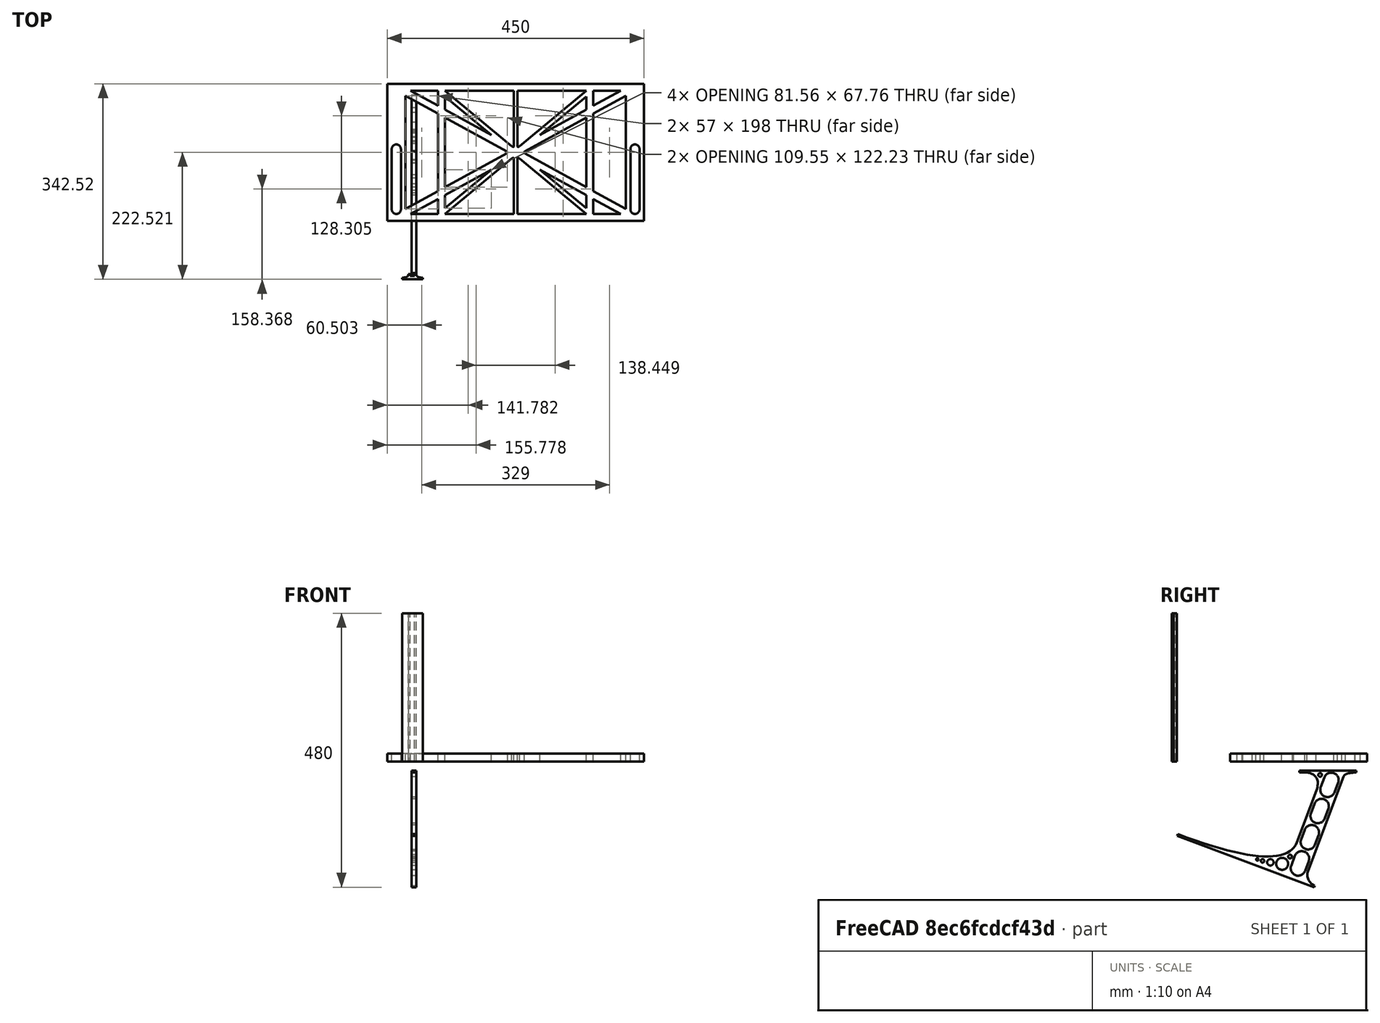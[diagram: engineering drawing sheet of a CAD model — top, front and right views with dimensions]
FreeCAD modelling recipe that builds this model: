
FCSTD DOCUMENT  (FreeCAD 0.19R0.19.2)
Label: laptopStand062
License: All rights reserved
LicenseURL: http://en.wikipedia.org/wiki/All_rights_reserved
objects: Sketcher::SketchObject×3, Part::Extrusion×3
note: 6 computed .brp shape members not serialized (recipe doc carries the construction recipe); baked Part::Feature solids carry a one-line shape summary decoded from their .brp

FEATURE [Sketcher::SketchObject] Sketch
  FullyConstrained = false
  sketch-geometry (100):
    g0: LineSegment StartX=375.073 StartY=115.221 StartZ=0 EndX=318.073 EndY=83.9235 EndZ=0
    g1: LineSegment StartX=-10.9272 StartY=-82.7794 StartZ=0 EndX=46.0728 EndY=-51.4823 EndZ=0
    g2: LineSegment StartX=366.073 StartY=-91.7794 StartZ=0 EndX=318.073 EndY=-65.424 EndZ=0
    g3: LineSegment StartX=-10.9272 StartY=77.3346 StartZ=0 EndX=-10.9272 EndY=-82.7794 EndZ=0
    g4: LineSegment StartX=375.073 StartY=-82.7794 StartZ=0 EndX=375.073 EndY=115.221 EndZ=0
    g5: LineSegment StartX=-1.92719 StartY=-91.7794 StartZ=0 EndX=46.0728 EndY=-91.7794 EndZ=0
    g6: LineSegment StartX=318.073 StartY=124.221 StartZ=0 EndX=366.073 EndY=124.221 EndZ=0
    g7: LineSegment StartX=306.073 StartY=-81.8102 StartZ=0 EndX=224.513 EndY=-14.0532 EndZ=0
    g8: LineSegment StartX=58.0728 StartY=114.251 StartZ=0 EndX=139.632 EndY=46.4944 EndZ=0
    g9: LineSegment StartX=306.073 StartY=124.221 StartZ=0 EndX=189.124 EndY=27.0628 EndZ=0
    g10: LineSegment StartX=58.0728 StartY=-91.7794 StartZ=0 EndX=175.022 EndY=5.37834 EndZ=0
    g11: LineSegment StartX=58.0728 StartY=-81.8102 StartZ=0 EndX=58.0728 EndY=-58.8351 EndZ=0
    g12: LineSegment StartX=318.073 StartY=124.221 StartZ=0 EndX=318.073 EndY=97.8651 EndZ=0
    g13: LineSegment StartX=306.073 StartY=114.251 StartZ=0 EndX=306.073 EndY=91.2763 EndZ=0
    g14: LineSegment StartX=224.513 StartY=46.4944 StartZ=0 EndX=306.073 EndY=114.251 EndZ=0
    g15: LineSegment StartX=175.022 StartY=27.0628 StartZ=0 EndX=58.0728 EndY=124.221 EndZ=0
    g16: LineSegment StartX=139.632 StartY=-14.0532 StartZ=0 EndX=58.0728 EndY=-81.8102 EndZ=0
    g17: LineSegment StartX=224.513 StartY=46.4944 StartZ=0 EndX=306.073 EndY=91.2763 EndZ=0
    g18: LineSegment StartX=139.632 StartY=-14.0532 StartZ=0 EndX=58.0728 EndY=-58.8351 EndZ=0
    g19: LineSegment StartX=189.124 StartY=5.37834 StartZ=0 EndX=306.073 EndY=-91.7794 EndZ=0
    g20: LineSegment StartX=306.073 StartY=77.3346 StartZ=0 EndX=306.073 EndY=-44.8935 EndZ=0
    g21: LineSegment StartX=318.073 StartY=83.9235 StartZ=0 EndX=318.073 EndY=-51.4823 EndZ=0
    g22: LineSegment StartX=318.073 StartY=97.8651 StartZ=0 EndX=366.073 EndY=124.221 EndZ=0
    g23: LineSegment StartX=306.073 StartY=-58.8351 StartZ=0 EndX=224.513 EndY=-14.0532 EndZ=0
    g24: LineSegment StartX=306.073 StartY=-58.8351 StartZ=0 EndX=306.073 EndY=-81.8102 EndZ=0
    g25: LineSegment StartX=318.073 StartY=-51.4823 StartZ=0 EndX=375.073 EndY=-82.7794 EndZ=0
    g26: LineSegment StartX=318.073 StartY=-65.424 StartZ=0 EndX=318.073 EndY=-91.7794 EndZ=0
    g27: LineSegment StartX=318.073 StartY=-91.7794 StartZ=0 EndX=366.073 EndY=-91.7794 EndZ=0
    g28: LineSegment StartX=58.0728 StartY=-44.8935 StartZ=0 EndX=58.0728 EndY=77.3346 EndZ=0
    g29: LineSegment StartX=46.0728 StartY=-65.424 StartZ=0 EndX=-1.92719 EndY=-91.7794 EndZ=0
    g30: LineSegment StartX=46.0728 StartY=-65.424 StartZ=0 EndX=46.0728 EndY=-91.7794 EndZ=0
    g31: LineSegment StartX=58.0728 StartY=91.2763 StartZ=0 EndX=58.0728 EndY=114.251 EndZ=0
    g32: LineSegment StartX=46.0728 StartY=77.3346 StartZ=0 EndX=46.0728 EndY=-51.4823 EndZ=0
    g33: LineSegment StartX=58.0728 StartY=91.2763 StartZ=0 EndX=139.632 EndY=46.4944 EndZ=0
    g34: LineSegment StartX=-42.9272 StartY=136.221 StartZ=0 EndX=-42.9272 EndY=-103.779 EndZ=0
    g35: LineSegment StartX=407.073 StartY=136.221 StartZ=0 EndX=407.073 EndY=-103.779 EndZ=0
    g36: LineSegment StartX=179.022 StartY=27.0628 StartZ=0 EndX=179.022 EndY=124.221 EndZ=0
    g37: LineSegment StartX=185.124 StartY=27.0628 StartZ=0 EndX=185.124 EndY=124.221 EndZ=0
    g38: ArcOfCircle CenterX=-26.9272 CenterY=22.1087 CenterZ=0 NormalX=0 NormalY=0 NormalZ=1 AngleXU=0 Radius=8 StartAngle=1e-16 EndAngle=3.14159
    g39: ArcOfCircle CenterX=-26.9272 CenterY=-83.7794 CenterZ=0 NormalX=0 NormalY=0 NormalZ=1 AngleXU=0 Radius=8 StartAngle=3.14159 EndAngle=6.28319
    g40: LineSegment StartX=-34.9272 StartY=22.1087 StartZ=0 EndX=-34.9272 EndY=-83.7794 EndZ=0
    g41: LineSegment StartX=-18.9272 StartY=22.1087 StartZ=0 EndX=-18.9272 EndY=-83.7794 EndZ=0
    g42: LineSegment StartX=185.124 StartY=-91.7794 StartZ=0 EndX=306.073 EndY=-91.7794 EndZ=0
    g43: LineSegment StartX=179.022 StartY=-91.7794 StartZ=0 EndX=58.0728 EndY=-91.7794 EndZ=0
    g44: LineSegment StartX=306.073 StartY=124.221 StartZ=0 EndX=185.124 EndY=124.221 EndZ=0
    g45: LineSegment StartX=179.022 StartY=124.221 StartZ=0 EndX=58.0728 EndY=124.221 EndZ=0
    g46: ArcOfCircle CenterX=391.073 CenterY=22.1087 CenterZ=0 NormalX=0 NormalY=0 NormalZ=1 AngleXU=0 Radius=8 StartAngle=-4.4e-15 EndAngle=3.14159
    g47: LineSegment StartX=399.073 StartY=22.1087 StartZ=0 EndX=399.073 EndY=-83.7794 EndZ=0
    g48: LineSegment StartX=383.073 StartY=22.1087 StartZ=0 EndX=383.073 EndY=-83.7794 EndZ=0
    g49: ArcOfCircle CenterX=391.073 CenterY=-83.7794 CenterZ=0 NormalX=0 NormalY=0 NormalZ=1 AngleXU=0 Radius=8 StartAngle=3.14159 EndAngle=6.28319
    g50: Circle CenterX=175.022 CenterY=27.0628 CenterZ=0 NormalX=0 NormalY=0 NormalZ=1 AngleXU=0 Radius=1
    g51: Circle CenterX=179.022 CenterY=24.8665 CenterZ=0 NormalX=0 NormalY=0 NormalZ=1 AngleXU=0 Radius=1
    g52: Circle CenterX=179.022 CenterY=27.0628 CenterZ=0 NormalX=0 NormalY=0 NormalZ=1 AngleXU=0 Radius=1
    g53: BSplineCurve PolesCount=3 KnotsCount=2 Degree=2 IsPeriodic=0
    g54: GeomPoint X=175.022 Y=27.0628 Z=0
    g55: GeomPoint X=179.022 Y=27.0628 Z=0
    g56: Circle CenterX=189.124 CenterY=27.0628 CenterZ=0 NormalX=0 NormalY=0 NormalZ=1 AngleXU=0 Radius=1
    g57: Circle CenterX=185.124 CenterY=24.8665 CenterZ=0 NormalX=0 NormalY=0 NormalZ=1 AngleXU=0 Radius=1
    g58: Circle CenterX=185.124 CenterY=27.0628 CenterZ=0 NormalX=0 NormalY=0 NormalZ=1 AngleXU=0 Radius=1
    g59: BSplineCurve PolesCount=3 KnotsCount=2 Degree=2 IsPeriodic=0
    g60: GeomPoint X=189.124 Y=27.0628 Z=0
    g61: GeomPoint X=185.124 Y=27.0628 Z=0
    g62: Circle CenterX=175.022 CenterY=5.37834 CenterZ=0 NormalX=0 NormalY=0 NormalZ=1 AngleXU=0 Radius=1
    g63: Circle CenterX=179.022 CenterY=7.57463 CenterZ=0 NormalX=0 NormalY=0 NormalZ=1 AngleXU=0 Radius=1
    g64: Circle CenterX=179.022 CenterY=5.34704 CenterZ=0 NormalX=0 NormalY=0 NormalZ=1 AngleXU=0 Radius=1
    g65: BSplineCurve PolesCount=3 KnotsCount=2 Degree=2 IsPeriodic=0
    g66: GeomPoint X=175.022 Y=5.37834 Z=0
    g67: GeomPoint X=179.022 Y=5.34704 Z=0
    g68: Circle CenterX=189.124 CenterY=5.37834 CenterZ=0 NormalX=0 NormalY=0 NormalZ=1 AngleXU=0 Radius=1
    g69: Circle CenterX=185.124 CenterY=7.57463 CenterZ=0 NormalX=0 NormalY=0 NormalZ=1 AngleXU=0 Radius=1
    g70: Circle CenterX=185.124 CenterY=5.34704 CenterZ=0 NormalX=0 NormalY=0 NormalZ=1 AngleXU=0 Radius=1
    g71: BSplineCurve PolesCount=3 KnotsCount=2 Degree=2 IsPeriodic=0
    g72: GeomPoint X=189.124 Y=5.37834 Z=0
    g73: GeomPoint X=185.124 Y=5.34704 Z=0
    g74: LineSegment StartX=179.022 StartY=5.34704 StartZ=0 EndX=179.022 EndY=-91.7794 EndZ=0
    g75: LineSegment StartX=185.124 StartY=-91.7794 StartZ=0 EndX=185.124 EndY=5.34704 EndZ=0
    g76: Circle CenterX=165.871 CenterY=18.1458 CenterZ=0 NormalX=0 NormalY=0 NormalZ=1 AngleXU=0 Radius=1
    g77: Circle CenterX=169.377 CenterY=16.2206 CenterZ=0 NormalX=0 NormalY=0 NormalZ=1 AngleXU=0 Radius=1
    g78: Circle CenterX=165.871 CenterY=14.2954 CenterZ=0 NormalX=0 NormalY=0 NormalZ=1 AngleXU=0 Radius=1
    g79: BSplineCurve PolesCount=3 KnotsCount=2 Degree=2 IsPeriodic=0
    g80: GeomPoint X=165.871 Y=18.1458 Z=0
    g81: GeomPoint X=165.871 Y=14.2954 Z=0
    g82: Circle CenterX=198.275 CenterY=18.1458 CenterZ=0 NormalX=0 NormalY=0 NormalZ=1 AngleXU=0 Radius=1
    g83: Circle CenterX=194.768 CenterY=16.2206 CenterZ=0 NormalX=0 NormalY=0 NormalZ=1 AngleXU=0 Radius=1
    g84: Circle CenterX=198.275 CenterY=14.2954 CenterZ=0 NormalX=0 NormalY=0 NormalZ=1 AngleXU=0 Radius=1
    g85: BSplineCurve PolesCount=3 KnotsCount=2 Degree=2 IsPeriodic=0
    g86: GeomPoint X=198.275 Y=18.1458 Z=0
    g87: GeomPoint X=198.275 Y=14.2954 Z=0
    g88: LineSegment StartX=165.871 StartY=18.1458 StartZ=0 EndX=58.0728 EndY=77.3346 EndZ=0
    g89: LineSegment StartX=58.0728 StartY=-44.8935 StartZ=0 EndX=165.871 EndY=14.2954 EndZ=0
    g90: LineSegment StartX=198.275 StartY=18.1458 StartZ=0 EndX=306.073 EndY=77.3346 EndZ=0
    g91: LineSegment StartX=198.275 StartY=14.2954 StartZ=0 EndX=306.073 EndY=-44.8935 EndZ=0
    g92: LineSegment StartX=407.073 StartY=-103.779 StartZ=0 EndX=-42.9272 EndY=-103.779 EndZ=0
    g93: LineSegment StartX=407.073 StartY=136.221 StartZ=0 EndX=-42.9272 EndY=136.221 EndZ=0
    g94: LineSegment StartX=-26.9272 StartY=136.221 StartZ=0 EndX=-26.9272 EndY=98.2206 EndZ=0
    g95: LineSegment StartX=46.0728 StartY=77.3346 StartZ=0 EndX=-10.9272 EndY=77.3346 EndZ=0
    g96: LineSegment StartX=46.0728 StartY=105.865 StartZ=0 EndX=31.5028 EndY=105.865 EndZ=0
    g97: LineSegment StartX=46.0728 StartY=124.221 StartZ=0 EndX=46.0728 EndY=105.865 EndZ=0
    g98: LineSegment StartX=-1.92719 StartY=124.221 StartZ=0 EndX=31.5028 EndY=105.865 EndZ=0
    g99: LineSegment StartX=46.0728 StartY=124.221 StartZ=0 EndX=-1.92719 EndY=124.221 EndZ=0
  constraints (185):
    c: Horizontal(g5)
    c: Horizontal(g6)
    c: Coincident(g33,g8)
    c: Coincident(g14,g17)
    c: Coincident(g18,g16)
    c: Coincident(g23,g7)
    c: Coincident(g14,g13)
    c: Tangent(g13,g20)
    c: Tangent(g12,g21)
    c: Coincident(g17,g13)
    c: Tangent(g17,g22)
    c: Coincident(g0,g21)
    c: Coincident(g24,g7)
    c: Tangent(g2,g23)
    c: Tangent(g20,g24)
    c: Coincident(g21,g25)
    c: Coincident(g26,g2)
    c: Tangent(g21,g26)
    c: Coincident(g16,g11)
    c: Tangent(g11,g28)
    c: Coincident(g18,g11)
    c: Tangent(g18,g29)
    c: Coincident(g30,g29)
    c: Coincident(g1,g32)
    c: Tangent(g28,g31)
    c: Coincident(g8,g31)
    c: Coincident(g33,g31)
    c: Block(g15)
    c: Block(g9)
    c: Block(g12)
    c: Block(g22)
    c: Block(g0)
    c: Block(g25)
    c: Block(g4)
    c: Block(g23)
    c: Block(g24)
    c: Block(g2)
    c: Block(g26)
    c: Block(g14)
    c: Block(g19)
    c: Block(g10)
    c: Block(g18)
    c: Block(g16)
    c: Block(g30)
    c: Block(g29)
    c: Block(g1)
    c: Block(g3)
    c: Block(g8)
    c: Block(g31)
    c: Block(g20)
    c: Block(g6)
    c: Block(g27)
    c: Block(g5)
    c: Vertical(g34)
    c: Vertical(g35)
    c: Block(g35)
    c: Block(g34)
    c: Vertical(g36)
    c: Vertical(g37)
    c: Block(g36)
    c: Block(g37)
    c: Tangent(g38,g41) = 1.5708
    c: Tangent(g38,g40) = -1.5708
    c: Tangent(g40,g39) = -1.5708
    c: Tangent(g41,g39) = 1.5708
    c: Vertical(g40)
    c: Equal(g38,g39)
    c: Block(g41)
    c: Block(g40)
    c: Coincident(g42,g19)
    c: Horizontal(g42)
    c: Coincident(g43,g10)
    c: Horizontal(g43)
    c: Coincident(g44,g9)
    c: Coincident(g44,g37)
    c: Horizontal(g44)
    c: Coincident(g45,g36)
    c: Coincident(g45,g15)
    c: Horizontal(g45)
    c: Tangent(g46,g47) = 1.5708
    c: Tangent(g47,g49) = 1.5708
    c: Equal(g46,g49)
    c: Coincident(g48,g46)
    c: Coincident(g48,g49)
    c: Block(g47)
    c: Block(g48)
    c: Coincident(g53,g15)
    c: Weight(g50) = 1
    c: Equal(g50,g51)
    c: Equal(g50,g52)
    c: Coincident(g53,g36)
    c: InternalAlignment(g50,g53)
    c: InternalAlignment(g51,g53)
    c: InternalAlignment(g52,g53)
    c: InternalAlignment(g54,g53)
    c: InternalAlignment(g55,g53)
    c: Coincident(g59,g9)
    c: Weight(g56) = 1
    c: Equal(g56,g57)
    c: Equal(g56,g58)
    c: Coincident(g59,g37)
    c: InternalAlignment(g56,g59)
    c: InternalAlignment(g57,g59)
    c: InternalAlignment(g58,g59)
    c: InternalAlignment(g60,g59)
    c: InternalAlignment(g61,g59)
    c: Block(g59)
    c: Block(g53)
    c: Coincident(g65,g10)
    c: Weight(g62) = 1
    c: Equal(g62,g63)
    c: Equal(g62,g64)
    c: InternalAlignment(g62,g65)
    c: InternalAlignment(g63,g65)
    c: InternalAlignment(g64,g65)
    c: InternalAlignment(g66,g65)
    c: InternalAlignment(g67,g65)
    c: Weight(g68) = 1
    c: Equal(g68,g69)
    c: Equal(g68,g70)
    c: InternalAlignment(g68,g71)
    c: InternalAlignment(g69,g71)
    c: InternalAlignment(g70,g71)
    c: InternalAlignment(g72,g71)
    c: InternalAlignment(g73,g71)
    c: Block(g71)
    c: Block(g65)
    c: Coincident(g74,g65)
    c: Coincident(g74,g43)
    c: Vertical(g74)
    c: Coincident(g75,g42)
    c: Coincident(g75,g71)
    c: Vertical(g75)
    c: Weight(g76) = 1
    c: Equal(g76,g77)
    c: Equal(g76,g78)
    c: InternalAlignment(g76,g79)
    c: InternalAlignment(g77,g79)
    c: InternalAlignment(g78,g79)
    c: InternalAlignment(g80,g79)
    c: InternalAlignment(g81,g79)
    c: Weight(g82) = 1
    c: Equal(g82,g83)
    c: Equal(g82,g84)
    c: InternalAlignment(g82,g85)
    c: InternalAlignment(g83,g85)
    c: InternalAlignment(g84,g85)
    c: InternalAlignment(g86,g85)
    c: InternalAlignment(g87,g85)
    c: Block(g79)
    c: Block(g85)
    c: Coincident(g88,g79)
    c: Coincident(g88,g28)
    c: Coincident(g89,g28)
    c: Coincident(g89,g79)
    c: Coincident(g90,g85)
    c: Coincident(g90,g20)
    c: Coincident(g91,g85)
    c: Coincident(g91,g20)
    c: Block(g28)
    c: Coincident(g92,g35)
    c: Coincident(g92,g34)
    c: Horizontal(g92)
    c: Distance(g92) = 450
    c: Coincident(g93,g35)
    c: Coincident(g93,g34)
    c: Horizontal(g93)
    c: PointOnObject(g94,g93)
    c: Vertical(g94)
    c: Distance(g94) = 38
    c: Horizontal(g95)
    c: Coincident(g32,g95)
    c: Horizontal(g96)
    c: Vertical(g97)
    c: Block(g97)
    c: Block(g96)
    c: Block(g95)
    c: Distance(g97) = 18.3554
    c: Coincident(g99,g97)
    c: Coincident(g99,g98)
    c: Horizontal(g99)
    c: Block(g99)
    c: Block(g98)
    c: Coincident(g96,g98)
    c: Coincident(g3,g95)
FEATURE [Sketcher::SketchObject] Sketch001
  FullyConstrained = true
  MapMode = 4
  Placement = pos=(0,0,0) rot=(0.57735,0.57735,0.57735;2.0944rad)
  Support = -> [Sketch]
  sketch-geometry (46):
    g0: BSplineCurve PolesCount=3 KnotsCount=2 Degree=2 IsPeriodic=0
    g1: ArcOfCircle CenterX=73.1223 CenterY=-32.291 CenterZ=0 NormalX=0 NormalY=0 NormalZ=1 AngleXU=0 Radius=13 StartAngle=5.92268 EndAngle=9.06428
    g2: ArcOfCircle CenterX=66.7816 CenterY=-49.1439 CenterZ=0 NormalX=0 NormalY=0 NormalZ=1 AngleXU=0 Radius=13 StartAngle=2.78068 EndAngle=5.92131
    g3: ArcOfCircle CenterX=55.9263 CenterY=-78.1807 CenterZ=0 NormalX=0 NormalY=0 NormalZ=1 AngleXU=0 Radius=13 StartAngle=5.92268 EndAngle=9.06428
    g4: ArcOfCircle CenterX=49.5884 CenterY=-95.0342 CenterZ=0 NormalX=0 NormalY=0 NormalZ=1 AngleXU=0 Radius=13 StartAngle=2.78068 EndAngle=5.92131
    g5: ArcOfCircle CenterX=38.7206 CenterY=-124.067 CenterZ=0 NormalX=0 NormalY=0 NormalZ=1 AngleXU=0 Radius=13 StartAngle=5.92268 EndAngle=9.06428
    g6: ArcOfCircle CenterX=32.3875 CenterY=-140.92 CenterZ=0 NormalX=0 NormalY=0 NormalZ=1 AngleXU=0 Radius=13 StartAngle=2.78068 EndAngle=5.92131
    g7: ArcOfCircle CenterX=21.4715 CenterY=-169.934 CenterZ=0 NormalX=0 NormalY=0 NormalZ=1 AngleXU=0 Radius=13 StartAngle=5.92268 EndAngle=9.06428
    g8: ArcOfCircle CenterX=15.1336 CenterY=-186.787 CenterZ=0 NormalX=0 NormalY=0 NormalZ=1 AngleXU=0 Radius=13 StartAngle=2.78068 EndAngle=5.92131
    g9-g12: Circle x4 (B-spline internal-alignment scaffolding for g13; pole/knot coordinates omitted)
    g13: BSplineCurve PolesCount=4 KnotsCount=2 Degree=3 IsPeriodic=0
    g14: GeomPoint X=28.8094 Y=-19.0875 Z=0
    g15: GeomPoint X=47.0443 Y=-50.4712 Z=0
    g16: Circle CenterX=53.5586 CenterY=-23.2695 CenterZ=0 NormalX=0 NormalY=0 NormalZ=1 AngleXU=0 Radius=3.24518
    g17: Circle CenterX=-195.441 CenterY=-127.082 CenterZ=0 NormalX=0 NormalY=0 NormalZ=1 AngleXU=0 Radius=1
    g18: Circle CenterX=-8.24091 CenterY=-197.481 CenterZ=0 NormalX=0 NormalY=0 NormalZ=1 AngleXU=0 Radius=1
    g19: Circle CenterX=12.8789 CenterY=-141.321 CenterZ=0 NormalX=0 NormalY=0 NormalZ=1 AngleXU=0 Radius=1
    g20: BSplineCurve PolesCount=3 KnotsCount=2 Degree=2 IsPeriodic=0
    g21: GeomPoint X=-195.441 Y=-127.082 Z=0
    g22: GeomPoint X=12.8789 Y=-141.321 Z=0
    g23: Circle CenterX=-12.8016 CenterY=-179.036 CenterZ=0 NormalX=0 NormalY=0 NormalZ=1 AngleXU=0 Radius=10.5072
    g24: Circle CenterX=0.933922 CenterY=-166.43 CenterZ=0 NormalX=0 NormalY=0 NormalZ=1 AngleXU=0 Radius=3.26661
    g25: Circle CenterX=-33.5518 CenterY=-176.44 CenterZ=0 NormalX=0 NormalY=0 NormalZ=1 AngleXU=0 Radius=5.64388
    g26: Circle CenterX=-47.2366 CenterY=-173.859 CenterZ=0 NormalX=0 NormalY=0 NormalZ=1 AngleXU=0 Radius=3.01653
    g27: Circle CenterX=-56.2595 CenterY=-171.456 CenterZ=0 NormalX=0 NormalY=0 NormalZ=1 AngleXU=0 Radius=2.12826
    g28: ArcOfCircle CenterX=51.2151 CenterY=-198.473 CenterZ=0 NormalX=0 NormalY=0 NormalZ=1 AngleXU=0 Radius=20 StartAngle=2.78189 EndAngle=4.35269
    g29: LineSegment StartX=32.4951 StartY=-191.433 StartZ=0 EndX=94.6578 EndY=-26.1352 EndZ=0
    g30: LineSegment StartX=43.1192 StartY=-220.001 StartZ=0 EndX=-196.497 EndY=-129.89 EndZ=0
    g31: LineSegment StartX=43.1192 StartY=-220.001 StartZ=0 EndX=44.1752 EndY=-217.193 EndZ=0
    g32: LineSegment StartX=117.223 StartY=-19.0875 StartZ=0 EndX=117.223 EndY=-16.0875 EndZ=0
    g33: LineSegment StartX=117.223 StartY=-16.0875 StartZ=0 EndX=17.2232 EndY=-16.0875 EndZ=0
    g34: LineSegment StartX=17.2232 StartY=-16.0875 StartZ=0 EndX=17.2232 EndY=-19.0875 EndZ=0
    g35: LineSegment StartX=28.8094 StartY=-19.0875 StartZ=0 EndX=17.2232 EndY=-19.0875 EndZ=0
    g36: LineSegment StartX=47.0443 StartY=-50.4712 StartZ=0 EndX=12.8789 EndY=-141.321 EndZ=0
    g37: LineSegment StartX=-195.441 StartY=-127.082 StartZ=0 EndX=-196.497 EndY=-129.89 EndZ=0
    g38: LineSegment StartX=85.2866 StartY=-36.8766 StartZ=0 EndX=78.9396 EndY=-53.7463 EndZ=0
    g39: LineSegment StartX=60.9579 StartY=-27.7053 StartZ=0 EndX=54.6191 EndY=-44.5532 EndZ=0
    g40: LineSegment StartX=68.0907 StartY=-82.7664 StartZ=0 EndX=61.7465 EndY=-99.6365 EndZ=0
    g41: LineSegment StartX=43.7619 StartY=-73.595 StartZ=0 EndX=37.426 EndY=-90.4435 EndZ=0
    g42: LineSegment StartX=50.885 StartY=-128.652 StartZ=0 EndX=44.5456 EndY=-145.522 EndZ=0
    g43: LineSegment StartX=26.5562 StartY=-119.481 StartZ=0 EndX=20.2251 EndY=-136.329 EndZ=0
    g44: LineSegment StartX=9.3071 StartY=-165.349 StartZ=0 EndX=2.97115 EndY=-182.197 EndZ=0
    g45: LineSegment StartX=33.6358 StartY=-174.52 StartZ=0 EndX=27.2917 EndY=-191.39 EndZ=0
  constraints (71):
    c: Block(g0)
    c: Block(g1)
    c: Block(g2)
    c: Block(g4)
    c: Block(g3)
    c: Block(g6)
    c: Block(g5)
    c: Block(g8)
    c: Block(g7)
    c: Weight(g9) = 1
    c: Equal(g9,g10)
    c: Equal(g9,g11)
    c: Equal(g9,g12)
    c: InternalAlignment(g9-g12 -> g13) x4
    c: InternalAlignment(g14,g13)
    c: InternalAlignment(g15,g13)
    c: Block(g16)
    c: Weight(g17) = 1
    c: Equal(g17,g18)
    c: Equal(g17,g19)
    c: InternalAlignment(g17,g20)
    c: InternalAlignment(g18,g20)
    c: InternalAlignment(g19,g20)
    c: InternalAlignment(g21,g20)
    c: InternalAlignment(g22,g20)
    c: Block(g20)
    c: Block(g23)
    c: Block(g24)
    c: Block(g25)
    c: Block(g26)
    c: Block(g27)
    c: Block(g28)
    c: Coincident(g29,g28)
    c: Coincident(g29,g0)
    c: Block(g13)
    c: Coincident(g31,g30)
    c: Coincident(g31,g28)
    c: Block(g31)
    c: Coincident(g32,g0)
    c: Vertical(g32)
    c: Coincident(g33,g32)
    c: Horizontal(g33)
    c: Coincident(g34,g33)
    c: Vertical(g34)
    c: Block(g33)
    c: Coincident(g35,g13)
    c: Coincident(g35,g34)
    c: Horizontal(g35)
    c: Coincident(g36,g13)
    c: Coincident(g36,g20)
    c: Coincident(g37,g20)
    c: Coincident(g37,g30)
    c: Block(g30)
    c: Coincident(g38,g1)
    c: Coincident(g38,g2)
    c: Coincident(g39,g1)
    c: Coincident(g39,g2)
    c: Coincident(g40,g3)
    c: Coincident(g40,g4)
    c: Coincident(g41,g3)
    c: Coincident(g41,g4)
    c: Coincident(g42,g5)
    c: Coincident(g42,g6)
    c: Coincident(g43,g5)
    c: Coincident(g43,g6)
    c: Coincident(g44,g7)
    c: Coincident(g44,g8)
    c: Coincident(g45,g7)
    c: Coincident(g45,g8)
    c: Distance(g30) = 256
    c: Distance(g33) = 100
FEATURE [Part::Extrusion] Extrude002
  Base = -> Sketch001
  Dir = (1,0,0)
  DirMode = 2
  FaceMakerClass = Part::FaceMakerBullseye
  LengthFwd = 8
  LengthRev = 0
  Solid = true
  Symmetric = false
FEATURE [Sketcher::SketchObject] Sketch002
  FullyConstrained = true
  sketch-geometry (20):
    g0: LineSegment StartX=-2.77179 StartY=-200.304 StartZ=0 EndX=5.22821 EndY=-200.304 EndZ=0
    g1: LineSegment StartX=5.22821 StartY=-200.304 StartZ=0 EndX=5.22821 EndY=-197.304 EndZ=0
    g2: LineSegment StartX=-2.77179 StartY=-200.304 StartZ=0 EndX=-2.77179 EndY=-197.304 EndZ=0
    g3: LineSegment StartX=5.22821 StartY=-197.304 StartZ=0 EndX=8.22821 EndY=-197.304 EndZ=0
    g4: LineSegment StartX=-2.77179 StartY=-197.304 StartZ=0 EndX=-5.77179 EndY=-197.304 EndZ=0
    g5: LineSegment StartX=19.2282 StartY=-203.304 StartZ=0 EndX=19.2282 EndY=-206.304 EndZ=0
    g6: LineSegment StartX=-16.7718 StartY=-203.304 StartZ=0 EndX=-16.7718 EndY=-206.304 EndZ=0
    g7: LineSegment StartX=-16.7718 StartY=-206.304 StartZ=0 EndX=19.2282 EndY=-206.304 EndZ=0
    g8: Circle CenterX=-16.7718 CenterY=-203.304 CenterZ=0 NormalX=0 NormalY=0 NormalZ=1 AngleXU=0 Radius=1
    g9: Circle CenterX=-5.77179 CenterY=-203.304 CenterZ=0 NormalX=0 NormalY=0 NormalZ=1 AngleXU=0 Radius=1
    g10: Circle CenterX=-5.77179 CenterY=-197.304 CenterZ=0 NormalX=0 NormalY=0 NormalZ=1 AngleXU=0 Radius=1
    g11: BSplineCurve PolesCount=3 KnotsCount=2 Degree=2 IsPeriodic=0
    g12: GeomPoint X=-16.7718 Y=-203.304 Z=0
    g13: GeomPoint X=-5.77179 Y=-197.304 Z=0
    g14: Circle CenterX=19.2282 CenterY=-203.304 CenterZ=0 NormalX=0 NormalY=0 NormalZ=1 AngleXU=0 Radius=1
    g15: Circle CenterX=8.22821 CenterY=-203.304 CenterZ=0 NormalX=0 NormalY=0 NormalZ=1 AngleXU=0 Radius=1
    g16: Circle CenterX=8.22821 CenterY=-197.304 CenterZ=0 NormalX=0 NormalY=0 NormalZ=1 AngleXU=0 Radius=1
    g17: BSplineCurve PolesCount=3 KnotsCount=2 Degree=2 IsPeriodic=0
    g18: GeomPoint X=19.2282 Y=-203.304 Z=0
    g19: GeomPoint X=8.22821 Y=-197.304 Z=0
  constraints (41):
    c: Horizontal(g0)
    c: Distance(g0) = 8
    c: Coincident(g1,g0)
    c: Vertical(g1)
    c: Distance(g1) = 3
    c: Coincident(g2,g0)
    c: Vertical(g2)
    c: Distance(g2) = 3
    c: Coincident(g3,g1)
    c: Horizontal(g3)
    c: Distance(g3) = 3
    c: Coincident(g4,g2)
    c: Horizontal(g4)
    c: Distance(g4) = 3
    c: Vertical(g5)
    c: Vertical(g6)
    c: Coincident(g7,g6)
    c: Coincident(g7,g5)
    c: Weight(g8) = 1
    c: Equal(g8,g9)
    c: Equal(g8,g10)
    c: Coincident(g11,g4)
    c: InternalAlignment(g8,g11)
    c: InternalAlignment(g9,g11)
    c: InternalAlignment(g10,g11)
    c: InternalAlignment(g12,g11)
    c: InternalAlignment(g13,g11)
    c: Coincident(g17,g5)
    c: Weight(g14) = 1
    c: Equal(g14,g15)
    c: Equal(g14,g16)
    c: Coincident(g17,g3)
    c: InternalAlignment(g14,g17)
    c: InternalAlignment(g15,g17)
    c: InternalAlignment(g16,g17)
    c: InternalAlignment(g18,g17)
    c: InternalAlignment(g19,g17)
    c: Block(g7)
    c: Block(g17)
    c: Block(g11)
    c: Block(g6)
FEATURE [Part::Extrusion] Extrude003
  Base = -> Sketch002
  Dir = (0,0,1)
  DirMode = 2
  FaceMakerClass = Part::FaceMakerBullseye
  LengthFwd = 260
  LengthRev = 0
  Solid = true
  Symmetric = false
FEATURE [Part::Extrusion] Extrude
  Base = -> Sketch
  Dir = (0,0,1)
  DirMode = 2
  FaceMakerClass = Part::FaceMakerBullseye
  LengthFwd = 14
  LengthRev = 0
  Solid = true
  Symmetric = false
